# Revit family: Standard-Range-Non-Condensing_84-87_Water-Heater_LOD200
name_source: partatom
category: Mechanical Equipment
revit_build: Autodesk Revit 2014 (Build: 20130308_1515(x64)
units: mm (PartAtom-declared; Revit-internal decimal feet)

## types (1)
- Standard-Range_84-87
    Access Clearance Bottom = 0 mm
    Access Clearance Front = 610 mm
    Access Clearance Left = 305 mm
    Access Clearance Rear = 305 mm
    Access Clearance Right = 305 mm
    Access Clearance Top = 1270 mm
    Air Inlet Connection Size = 0 mm
    Air Inlet Connection Type = External
    BMS Links = Yes
    CE Approval = Yes - 63AP0271
    Clean Out and Inspection Opening Type = Flanged
    Colour = Grey (RAL 7047)
    Condensate Drain Size = 0 mm
    Condensing = No
    Continuous Output at 44 Degree Differential l/h = 395
    Continuous Output at 50 Degree Differential l/h = 348
    Control Thermostat Range Note = 40 to 70
    Control ThermostatRange = 40 °F
    Control Type = Internal
    Drain Connection Size = 19 mm
    Drain Connection Type = Threaded
    Emissions mg/kWh = 78
    Enclosure Rating = 20
    Energy Technology List = No
    ErP Energy Label = Yes
    External Material = Aluminium
    Features = Open Flue Atmospheric Natural Draught Heater
    Finish = Painted
    Flow and Return Connection Size = 32 mm
    Flow and Return Connection Type = Threaded
    Flue Connection Note = 80mm / 125mm
    Flue Connection Radius = 63 mm
    Flue Connection Size = 125 mm
    Flue Connection Type = External
    Flue or Air Intake Classification = B11
    Frequency = 50 Hz
    Fuel = Gas - NG
    Fuel Connection Size = 13 mm
    Fuel Connection Type = Socket
    Full Load Current = 3 A
    Fuse Rating = 5 A
    Gas Consumption rate = 2 CFM
    Gas Flow Rate = 2 CFM
    Gross Input Of Appliance = 26 Btu/h
    Gross Weight = 181.00 kg
    Heat Exchanger Material = Steel Glass Lined
    Heat Generator Efficiency = 78.1
    Heat Loss kWh/24h = 254
    Heat Up Time mins = 66
    Insulation Thickness = 50 mm
    Insulation Type = Foam Injected
    Interlocks = Yes
    Manufacturer = Andrews Water Heaters
    Max Operating Pressure When Open Vented = 10.00 psi
    Max Operating Pressure When Unvented = 3.50 psi
    Maximum Gas Inlet Pressure mbar = 40
    Maximum Oil Inlet Pressure mbar = 0
    Maximum Power Consumption = 236 W
    Maximum Starting Current = 3 A
    Maximum Water Temperature = 71 °F
    Min Operating Pressure mbar = 0.2
    Minimum Gas Inlet Pressure mbar = 18
    Minimum Oil Inlet Pressure mbar = 0
    Minimum Power Consumption = 236 W
    Model = 84/87
    Mounting = Floor Standing
    Nett Weight = 562.00 kg
    Nominal Gas Inlet Pressure = 21
    Nominal Oil Inlet Pressure mbar = 0
    O&M Manual = http://www.andrewswaterheaters.co.uk
    Oil Consumption Rate l/h = 0
    Oil Flow Rate kg/h = 0
    Operation = On/Off
    Overall Diameter = 718 mm
    Overall Height = 1788 mm
    Overall Length = 0 mm
    Overall Width = 0 mm
    Power Consumption of Shunt Pump = 0 W
    Product Literature = http://www.andrewswaterheaters.co.uk
    Product Range = Standard Range
    Recovery Rate litre/min = 5.8
    Reference Standard = BSE 89
    Responsible Extraction of Materials = Yes
    Safety Valve Connection Size = 19 mm
    Safety Valve Connection Type = Threaded
    Secondary Return Connection Size = 19 mm
    Secondary Return Connection Type = Threaded
    Shape = Cylindrical (Vertical)
    Shipping Carton Height = 1829 mm
    Shipping Carton Length = 914 mm
    Shipping Carton Width = 762 mm
    Shipping Weight = 194.00 kg
    Storage Capacity = 382.00 L
    Supply Phase = Single Phase
    Type = Direct Gas Fired Water Heater
    URL = http://www.andrewswaterheaters.co.uk
    Voltage = 240 V

## geometry (parser evidence)
native form markers: Blend x6, Extrusion x1, Sweep x11
no freeform markers — native parametric forms only
